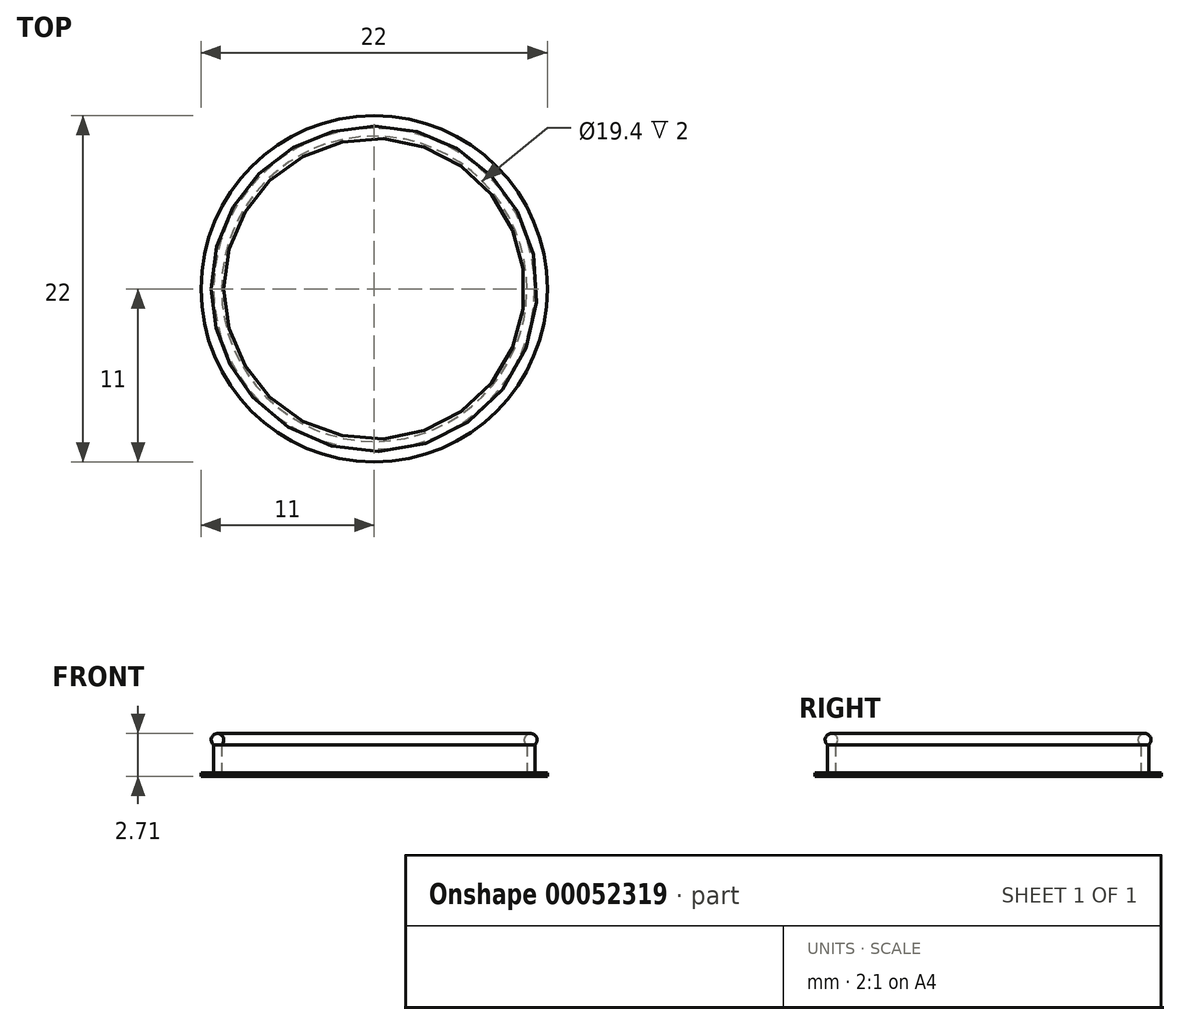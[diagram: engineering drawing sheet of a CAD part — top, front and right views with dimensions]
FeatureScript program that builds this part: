
annotation { "Feature Type Name" : "Feature", "Feature Type Description" : "" }
export const myFeature = defineFeature(function(context is Context, id is Id, definition is map)
    precondition{}
    {
        {
            var Q0;
            Q0=qCreatedBy(makeId("Front.planeOp"),FACE);
            var sketch = newSketch(context, id + "F0", { "sketchPlane" : qUnion([Q0])});
            skLineSegment(sketch, "E0", {"start": v(9.7, 2) * mm, "end": v(9.7, 0) * mm});
            skLineSegment(sketch, "E1", {"start": v(9.7, 0) * mm, "end": v(11, 0) * mm});
            skLineSegment(sketch, "E2", {"start": v(11, 0) * mm, "end": v(11, 0.2) * mm});
            skLineSegment(sketch, "E3", {"start": v(11, 0.2) * mm, "end": v(10.2, 0.2) * mm});
            skLineSegment(sketch, "E4", {"start": v(10.2, 0.2) * mm, "end": v(10.2, 2) * mm});
            skArc(sketch, "E5", {"start": v(10.2, 2) * mm, "mid": v(9.95, 2.71) * mm, "end": v(9.7, 2) * mm});
            skLineSegment(sketch, "E6", {"start": v(0, 0) * mm, "end": v(0, 12.05) * mm});
            skSolve(sketch);
        }
        {
            var Q0;
            Q0=makeQuery(id+"F0.imprint","IMPRINT",FACE,{"disambiguationData":[TD([[makeQuery(id+"F0.imprint","IMPRINT",EDGE,{"derivedFrom":sQuery(id+"F0.wireOp",EDGE,"E0")}),1.0]])]});
            var Q1;
            Q1=sQuery(id+"F0.wireOp",EDGE,"E6");
            revolve(context, id + "F1", {"entities" : qUnion([Q0]), "axis" : qUnion([Q1]), "revolveType" : RevolveType.FULL});
        }
    });
